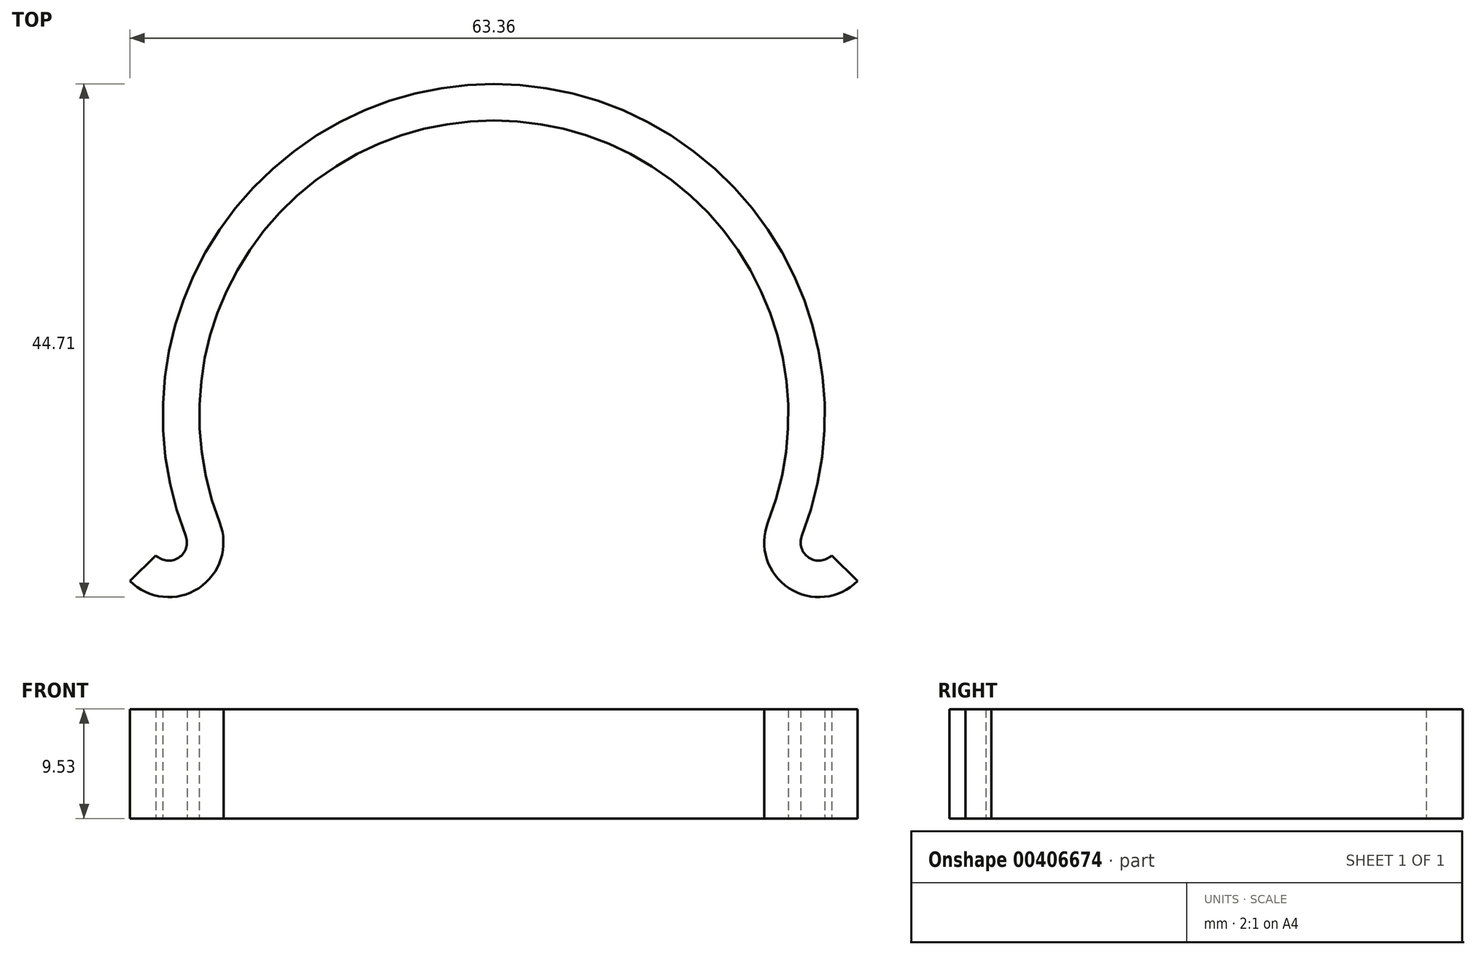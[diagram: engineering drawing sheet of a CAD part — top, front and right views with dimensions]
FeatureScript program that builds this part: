
annotation { "Feature Type Name" : "Feature", "Feature Type Description" : "" }
export const myFeature = defineFeature(function(context is Context, id is Id, definition is map)
    precondition{}
    {
        {
            var Q0;
            Q0=qCreatedBy(makeId("Top.planeOp"),FACE);
            var sketch = newSketch(context, id + "F0", { "sketchPlane" : qUnion([Q0])});
            skArc(sketch, "E0", {"start": v(23.88, -9.37) * mm, "mid": v(0, 25.65) * mm, "end": v(-23.88, -9.37) * mm});
            skLineSegment(sketch, "E1", {"start": v(-51.24, -15.88) * mm, "end": v(46.19, -15.88) * mm, "construction": true});
            skArc(sketch, "E2", {"start": v(23.88, -9.37) * mm, "mid": v(25.7, -15.1) * mm, "end": v(31.68, -14.48) * mm});
            skArc(sketch, "E3", {"start": v(-31.68, -14.48) * mm, "mid": v(-25.7, -15.1) * mm, "end": v(-23.88, -9.37) * mm});
            skLineSegment(sketch, "E4", {"start": v(28.31, -11.11) * mm, "end": v(28.31, -15.88) * mm, "construction": true});
            skLineSegment(sketch, "E5", {"start": v(-28.31, -11.11) * mm, "end": v(-28.31, -15.88) * mm, "construction": true});
            skLineSegment(sketch, "E6", {"start": v(-28.31, -11.11) * mm, "end": v(-39.44, -22.24) * mm, "construction": true});
            skLineSegment(sketch, "E7", {"start": v(28.31, -11.11) * mm, "end": v(40.79, -23.59) * mm, "construction": true});
            skArc(sketch, "E8", {"start": v(-29.43, -12.24) * mm, "mid": v(-27.44, -12.44) * mm, "end": v(-26.83, -10.53) * mm});
            skLineSegment(sketch, "E9", {"start": v(-31.68, -14.48) * mm, "end": v(-29.43, -12.24) * mm});
            skArc(sketch, "E10", {"start": v(26.83, -10.53) * mm, "mid": v(27.44, -12.44) * mm, "end": v(29.43, -12.24) * mm});
            skLineSegment(sketch, "E11", {"start": v(31.68, -14.48) * mm, "end": v(29.43, -12.24) * mm});
            skArc(sketch, "E12", {"start": v(26.83, -10.53) * mm, "mid": v(0, 28.83) * mm, "end": v(-26.83, -10.53) * mm});
            skSolve(sketch);
        }
        {
            var Q0;
            Q0=makeQuery(id+"F0.imprint","IMPRINT",FACE,{"disambiguationData":[TD([[makeQuery(id+"F0.imprint","IMPRINT",EDGE,{"derivedFrom":sQuery(id+"F0.wireOp",EDGE,"E0")}),-1.0]])]});
            extrude(context, id + "F1", {"entities" : qUnion([Q0]), "depth" : 9.52 * mm});
        }
    });
